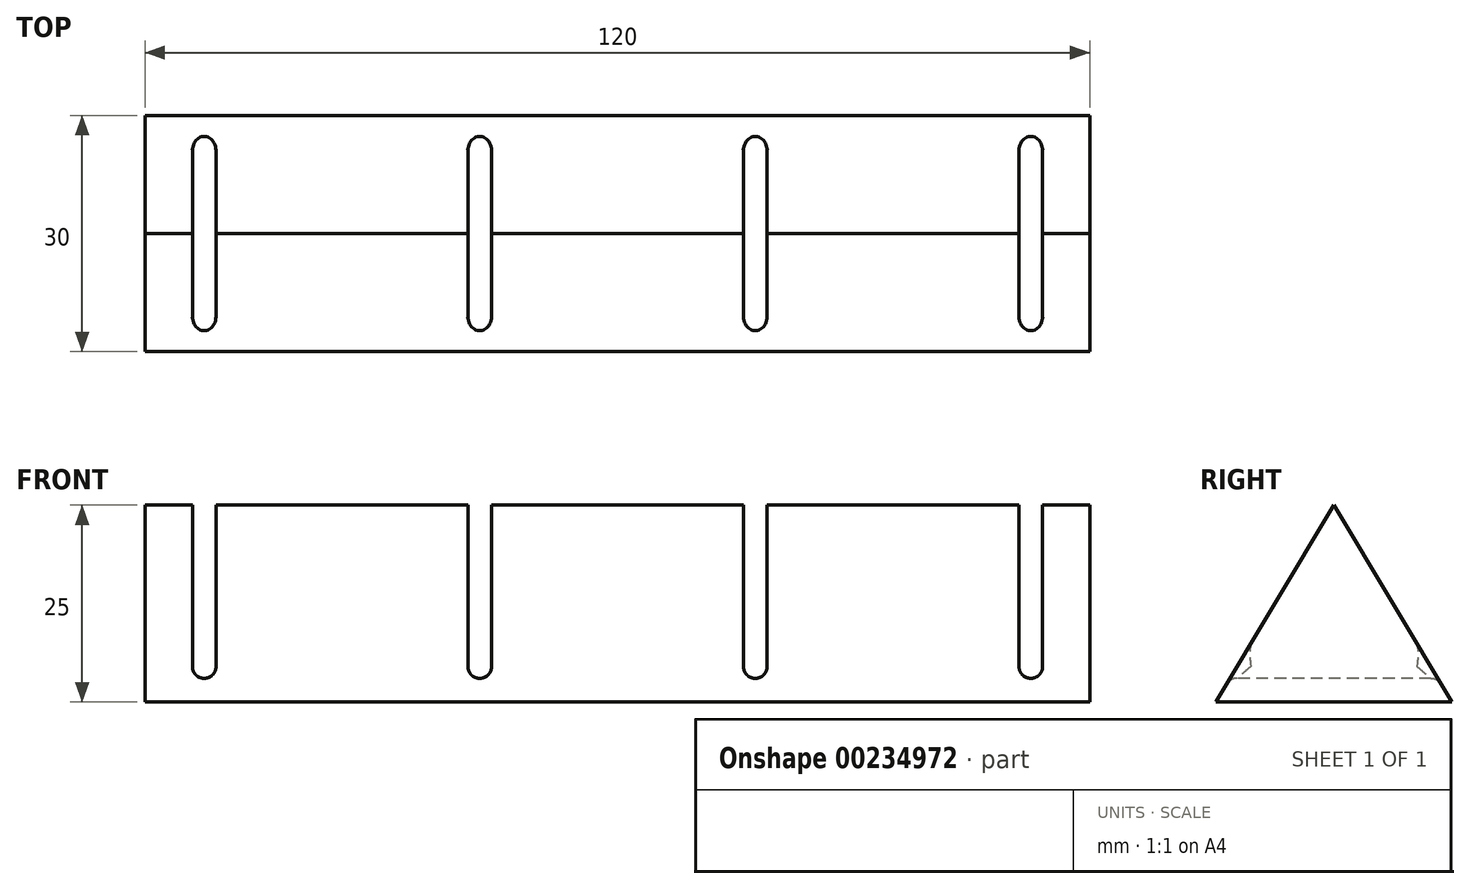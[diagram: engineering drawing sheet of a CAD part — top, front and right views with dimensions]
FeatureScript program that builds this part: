
annotation { "Feature Type Name" : "Feature", "Feature Type Description" : "" }
export const myFeature = defineFeature(function(context is Context, id is Id, definition is map)
    precondition{}
    {
        {
            var Q0;
            Q0=qCreatedBy(makeId("Top.planeOp"),FACE);
            var sketch = newSketch(context, id + "F0", { "sketchPlane" : qUnion([Q0])});
            skLineSegment(sketch, "E0.bottom", {"start": v(60, 15) * mm, "end": v(-60, 15) * mm});
            skLineSegment(sketch, "E0.top", {"start": v(60, -15) * mm, "end": v(-60, -15) * mm});
            skLineSegment(sketch, "E0.left", {"start": v(60, 15) * mm, "end": v(60, -15) * mm});
            skLineSegment(sketch, "E0.right", {"start": v(-60, 15) * mm, "end": v(-60, -15) * mm});
            skPoint(sketch, "E0.middle", {"position": v(0, 0) * mm});
            skSolve(sketch);
        }
        {
            var Q0;
            Q0=makeQuery(id+"F0.imprint","IMPRINT",FACE,{"disambiguationData":[TD([[makeQuery(id+"F0.imprint","IMPRINT",EDGE,{"derivedFrom":sQuery(id+"F0.wireOp",EDGE,"E0.bottom")}),1.0]])]});
            extrude(context, id + "F1", {"entities" : qUnion([Q0]), "depth" : 25 * mm});
        }
        {
            var Q0;
            Q0=makeQuery(id+"F1.opExtrude","SWEPT_FACE",FACE,{"disambiguationData":[OSD([sQuery(id+"F0.wireOp",EDGE,"E0.top")])]});
            var sketch = newSketch(context, id + "F2", { "sketchPlane" : qUnion([Q0])});
            skLineSegment(sketch, "E1.bottom", {"start": v(-54, 25) * mm, "end": v(-51, 25) * mm});
            skLineSegment(sketch, "E1.top", {"start": v(-54, 3) * mm, "end": v(-51, 3) * mm});
            skLineSegment(sketch, "E1.left", {"start": v(-54, 25) * mm, "end": v(-54, 3) * mm});
            skLineSegment(sketch, "E1.right", {"start": v(-51, 25) * mm, "end": v(-51, 3) * mm});
            skLineSegment(sketch, "E2.1.0.0", {"start": v(-16, 25) * mm, "end": v(-16, 3) * mm});
            skLineSegment(sketch, "E2.1.0.1", {"start": v(-19, 25) * mm, "end": v(-19, 3) * mm});
            skLineSegment(sketch, "E2.1.0.2", {"start": v(-19, 3) * mm, "end": v(-16, 3) * mm});
            skLineSegment(sketch, "E2.2.0.0", {"start": v(19, 25) * mm, "end": v(19, 3) * mm});
            skLineSegment(sketch, "E2.2.0.1", {"start": v(16, 25) * mm, "end": v(16, 3) * mm});
            skLineSegment(sketch, "E2.2.0.2", {"start": v(16, 3) * mm, "end": v(19, 3) * mm});
            skLineSegment(sketch, "E2.3.0.0", {"start": v(54, 25) * mm, "end": v(54, 3) * mm});
            skLineSegment(sketch, "E2.3.0.1", {"start": v(51, 25) * mm, "end": v(51, 3) * mm});
            skLineSegment(sketch, "E2.3.0.2", {"start": v(51, 3) * mm, "end": v(54, 3) * mm});
            skLineSegment(sketch, "E2.direction1", {"start": v(-51, 3) * mm, "end": v(-16, 3) * mm, "construction": true});
            skSolve(sketch);
        }
        {
            var Q0;
            Q0=makeQuery(id+"F2.imprint","IMPRINT",FACE,{"disambiguationData":[TD([[makeQuery(id+"F2.imprint","IMPRINT",EDGE,{"derivedFrom":sQuery(id+"F2.wireOp",EDGE,"E1.bottom")}),1.0]])]});
            var Q1;
            {var subQ0=sQuery(id+"F2.wireOp",EDGE,"E2.1.0.0");Q1=makeQuery(id+"F2.imprint","IMPRINT",FACE,{"disambiguationData":[TD([[makeQuery(id+"F2.imprint","IMPRINT",EDGE,{"derivedFrom":subQ0}),-1.0]])]});}
            var Q2;
            {var subQ0=sQuery(id+"F2.wireOp",EDGE,"E2.2.0.0");Q2=makeQuery(id+"F2.imprint","IMPRINT",FACE,{"disambiguationData":[TD([[makeQuery(id+"F2.imprint","IMPRINT",EDGE,{"derivedFrom":subQ0}),-1.0]])]});}
            var Q3;
            {var subQ0=sQuery(id+"F2.wireOp",EDGE,"E2.3.0.0");Q3=makeQuery(id+"F2.imprint","IMPRINT",FACE,{"disambiguationData":[TD([[makeQuery(id+"F2.imprint","IMPRINT",EDGE,{"derivedFrom":subQ0}),-1.0]])]});}
            extrude(context, id + "F3", {"entities" : qUnion([Q0, Q1, Q2, Q3]), "operationType" : NewBodyOperationType.REMOVE, "oppositeDirection" : true, "depth" : 30 * mm});
        }
        {
            var Q0;
            Q0=makeQuery(id+"F1.opExtrude","SWEPT_FACE",FACE,{"disambiguationData":[OSD([sQuery(id+"F0.wireOp",EDGE,"E0.right")])]});
            var sketch = newSketch(context, id + "F4", { "sketchPlane" : qUnion([Q0])});
            skLineSegment(sketch, "E3", {"start": v(-15, 0) * mm, "end": v(0, 25) * mm});
            skLineSegment(sketch, "E4", {"start": v(0, 25) * mm, "end": v(15, 0) * mm});
            skLineSegment(sketch, "E5", {"start": v(15, 0) * mm, "end": v(15, 25) * mm});
            skLineSegment(sketch, "E6", {"start": v(15, 25) * mm, "end": v(-15, 25) * mm});
            skLineSegment(sketch, "E7", {"start": v(-15, 25) * mm, "end": v(-15, 0) * mm});
            skSolve(sketch);
        }
        {
            var Q0;
            {var subQ0=sQuery(id+"F4.wireOp",EDGE,"E3");Q0=makeQuery(id+"F4.imprint","IMPRINT",FACE,{"disambiguationData":[TD([[makeQuery(id+"F4.imprint","IMPRINT",EDGE,{"derivedFrom":subQ0}),1.0]])]});}
            var Q1;
            {var subQ0=sQuery(id+"F4.wireOp",EDGE,"E4");Q1=makeQuery(id+"F4.imprint","IMPRINT",FACE,{"disambiguationData":[TD([[makeQuery(id+"F4.imprint","IMPRINT",EDGE,{"derivedFrom":subQ0}),1.0]])]});}
            extrude(context, id + "F5", {"entities" : qUnion([Q0, Q1]), "operationType" : NewBodyOperationType.REMOVE, "oppositeDirection" : true, "depth" : 120 * mm});
        }
        {
            var Q0;
            {var subQ0=sQuery(id+"F4.wireOp",EDGE,"E6");var subQ1=sQuery(id+"F4.wireOp",EDGE,"E4");var subQ2=sQuery(id+"F4.wireOp",EDGE,"E3");Q0=makeQuery(id+"F5.boolean.opBoolean","TWEAK_EDGE",EDGE,{"disambiguationData":[OD(1.0)],"derivedFrom":[makeQuery(id+"F5.opExtrude","SWEPT_EDGE",EDGE,{"disambiguationData":[OSD([subQ2,subQ1,subQ0]),ownerDisambiguation([makeQuery(id+"F5.opExtrude","SWEPT_BODY",BODY,{"disambiguationData":[OSD([subQ2,subQ0,sQuery(id+"F4.wireOp",EDGE,"E7")])]})])]}),makeQuery(id+"F5.opExtrude","SWEPT_EDGE",EDGE,{"disambiguationData":[OSD([subQ2,subQ1,subQ0]),ownerDisambiguation([makeQuery(id+"F5.opExtrude","SWEPT_BODY",BODY,{"disambiguationData":[OSD([subQ1,sQuery(id+"F4.wireOp",EDGE,"E5"),subQ0])]})])]})]});}
            var Q1;
            {var subQ0=sQuery(id+"F4.wireOp",EDGE,"E6");var subQ1=sQuery(id+"F4.wireOp",EDGE,"E4");var subQ2=sQuery(id+"F4.wireOp",EDGE,"E3");Q1=makeQuery(id+"F5.boolean.opBoolean","TWEAK_EDGE",EDGE,{"disambiguationData":[OD(4.0)],"derivedFrom":[makeQuery(id+"F5.opExtrude","SWEPT_EDGE",EDGE,{"disambiguationData":[OSD([subQ2,subQ1,subQ0]),ownerDisambiguation([makeQuery(id+"F5.opExtrude","SWEPT_BODY",BODY,{"disambiguationData":[OSD([subQ2,subQ0,sQuery(id+"F4.wireOp",EDGE,"E7")])]})])]}),makeQuery(id+"F5.opExtrude","SWEPT_EDGE",EDGE,{"disambiguationData":[OSD([subQ2,subQ1,subQ0]),ownerDisambiguation([makeQuery(id+"F5.opExtrude","SWEPT_BODY",BODY,{"disambiguationData":[OSD([subQ1,sQuery(id+"F4.wireOp",EDGE,"E5"),subQ0])]})])]})]});}
            var Q2;
            {var subQ0=sQuery(id+"F4.wireOp",EDGE,"E6");var subQ1=sQuery(id+"F4.wireOp",EDGE,"E4");var subQ2=sQuery(id+"F4.wireOp",EDGE,"E3");Q2=makeQuery(id+"F5.boolean.opBoolean","TWEAK_EDGE",EDGE,{"disambiguationData":[OD(3.0)],"derivedFrom":[makeQuery(id+"F5.opExtrude","SWEPT_EDGE",EDGE,{"disambiguationData":[OSD([subQ2,subQ1,subQ0]),ownerDisambiguation([makeQuery(id+"F5.opExtrude","SWEPT_BODY",BODY,{"disambiguationData":[OSD([subQ2,subQ0,sQuery(id+"F4.wireOp",EDGE,"E7")])]})])]}),makeQuery(id+"F5.opExtrude","SWEPT_EDGE",EDGE,{"disambiguationData":[OSD([subQ2,subQ1,subQ0]),ownerDisambiguation([makeQuery(id+"F5.opExtrude","SWEPT_BODY",BODY,{"disambiguationData":[OSD([subQ1,sQuery(id+"F4.wireOp",EDGE,"E5"),subQ0])]})])]})]});}
            var Q3;
            {var subQ0=sQuery(id+"F4.wireOp",EDGE,"E6");var subQ1=sQuery(id+"F4.wireOp",EDGE,"E4");var subQ2=sQuery(id+"F4.wireOp",EDGE,"E3");Q3=makeQuery(id+"F5.boolean.opBoolean","TWEAK_EDGE",EDGE,{"disambiguationData":[OD(2.0)],"derivedFrom":[makeQuery(id+"F5.opExtrude","SWEPT_EDGE",EDGE,{"disambiguationData":[OSD([subQ2,subQ1,subQ0]),ownerDisambiguation([makeQuery(id+"F5.opExtrude","SWEPT_BODY",BODY,{"disambiguationData":[OSD([subQ2,subQ0,sQuery(id+"F4.wireOp",EDGE,"E7")])]})])]}),makeQuery(id+"F5.opExtrude","SWEPT_EDGE",EDGE,{"disambiguationData":[OSD([subQ2,subQ1,subQ0]),ownerDisambiguation([makeQuery(id+"F5.opExtrude","SWEPT_BODY",BODY,{"disambiguationData":[OSD([subQ1,sQuery(id+"F4.wireOp",EDGE,"E5"),subQ0])]})])]})]});}
            var Q4;
            {var subQ0=sQuery(id+"F4.wireOp",EDGE,"E6");var subQ1=sQuery(id+"F4.wireOp",EDGE,"E4");var subQ2=sQuery(id+"F4.wireOp",EDGE,"E3");Q4=makeQuery(id+"F5.boolean.opBoolean","TWEAK_EDGE",EDGE,{"disambiguationData":[OD(0.0)],"derivedFrom":[makeQuery(id+"F5.opExtrude","SWEPT_EDGE",EDGE,{"disambiguationData":[OSD([subQ2,subQ1,subQ0]),ownerDisambiguation([makeQuery(id+"F5.opExtrude","SWEPT_BODY",BODY,{"disambiguationData":[OSD([subQ2,subQ0,sQuery(id+"F4.wireOp",EDGE,"E7")])]})])]}),makeQuery(id+"F5.opExtrude","SWEPT_EDGE",EDGE,{"disambiguationData":[OSD([subQ2,subQ1,subQ0]),ownerDisambiguation([makeQuery(id+"F5.opExtrude","SWEPT_BODY",BODY,{"disambiguationData":[OSD([subQ1,sQuery(id+"F4.wireOp",EDGE,"E5"),subQ0])]})])]})]});}
            var Q5;
            Q5=makeQuery(id+"F3.boolean.opBoolean","COPY",FACE,{"derivedFrom":makeQuery(id+"F3.opExtrude","SWEPT_FACE",FACE,{"disambiguationData":[OSD([sQuery(id+"F2.wireOp",EDGE,"E1.top")])]})});
            var Q6;
            Q6=makeQuery(id+"F3.boolean.opBoolean","COPY",FACE,{"derivedFrom":makeQuery(id+"F3.opExtrude","SWEPT_FACE",FACE,{"disambiguationData":[OSD([sQuery(id+"F2.wireOp",EDGE,"E2.1.0.2")])]})});
            var Q7;
            Q7=makeQuery(id+"F3.boolean.opBoolean","COPY",FACE,{"derivedFrom":makeQuery(id+"F3.opExtrude","SWEPT_FACE",FACE,{"disambiguationData":[OSD([sQuery(id+"F2.wireOp",EDGE,"E2.2.0.2")])]})});
            var Q8;
            Q8=makeQuery(id+"F3.boolean.opBoolean","COPY",FACE,{"derivedFrom":makeQuery(id+"F3.opExtrude","SWEPT_FACE",FACE,{"disambiguationData":[OSD([sQuery(id+"F2.wireOp",EDGE,"E2.3.0.2")])]})});
            var Q9;
            Q9=makeQuery(id+"F5.boolean.opBoolean","COPY",EDGE,{"derivedFrom":makeQuery(id+"F5.opExtrude","CAP_EDGE",EDGE,{"disambiguationData":[OSD([sQuery(id+"F4.wireOp",EDGE,"E3")])],"isStart":true})});
            var Q10;
            Q10=makeQuery(id+"F5.boolean.opBoolean","COPY",EDGE,{"derivedFrom":makeQuery(id+"F5.opExtrude","CAP_EDGE",EDGE,{"disambiguationData":[OSD([sQuery(id+"F4.wireOp",EDGE,"E4")])],"isStart":true})});
            var Q11;
            Q11=makeQuery(id+"F5.boolean.opBoolean","COPY",EDGE,{"derivedFrom":makeQuery(id+"F5.opExtrude","CAP_EDGE",EDGE,{"disambiguationData":[OSD([sQuery(id+"F4.wireOp",EDGE,"E4")])],"isStart":false})});
            var Q12;
            Q12=makeQuery(id+"F5.boolean.opBoolean","COPY",EDGE,{"derivedFrom":makeQuery(id+"F5.opExtrude","CAP_EDGE",EDGE,{"disambiguationData":[OSD([sQuery(id+"F4.wireOp",EDGE,"E3")])],"isStart":false})});
            fillet(context, id + "F6", {"entities" : qUnion([Q0, Q1, Q2, Q3, Q4, Q5, Q6, Q7, Q8, Q9, Q10, Q11, Q12]), "radius" : 1.5 * mm, "tangentPropagation" : true, "allowEdgeOverflow" : false});
        }
    });
